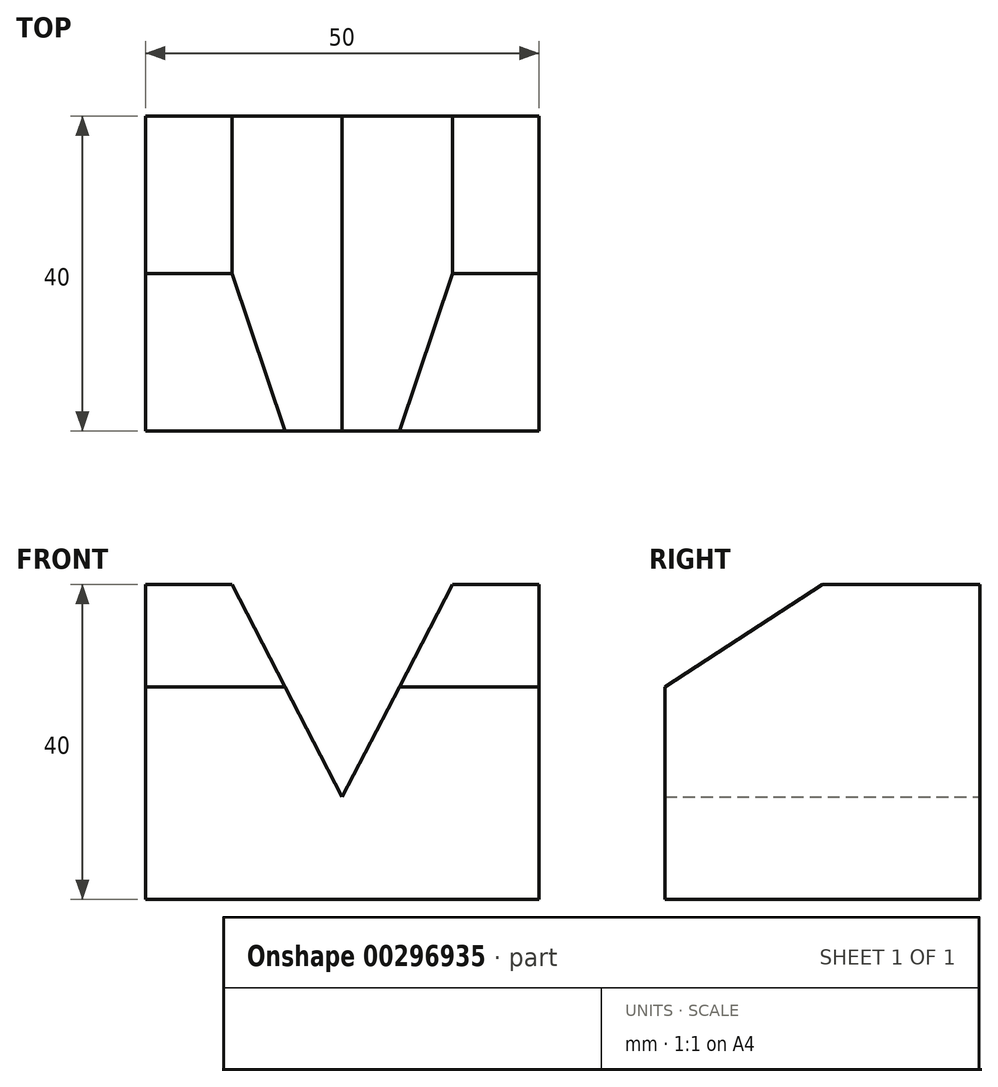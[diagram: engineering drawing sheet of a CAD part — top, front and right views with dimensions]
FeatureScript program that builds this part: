
annotation { "Feature Type Name" : "Feature", "Feature Type Description" : "" }
export const myFeature = defineFeature(function(context is Context, id is Id, definition is map)
    precondition{}
    {
        {
            var Q0;
            Q0=qCreatedBy(makeId("Right.planeOp"),FACE);
            var sketch = newSketch(context, id + "F0", { "sketchPlane" : qUnion([Q0])});
            skLineSegment(sketch, "E0.bottom", {"start": v(0, 0) * mm, "end": v(40, 0) * mm});
            skLineSegment(sketch, "E0.top", {"start": v(0, 40) * mm, "end": v(40, 40) * mm});
            skLineSegment(sketch, "E0.left", {"start": v(0, 0) * mm, "end": v(0, 40) * mm});
            skLineSegment(sketch, "E0.right", {"start": v(40, 0) * mm, "end": v(40, 40) * mm});
            skLineSegment(sketch, "E1", {"start": v(20, 40) * mm, "end": v(0, 27) * mm});
            skSolve(sketch);
        }
        {
            var Q0;
            {var subQ1=sQuery(id+"F0.wireOp",EDGE,"E0.bottom");Q0=makeQuery(id+"F0.imprint","IMPRINT",FACE,{"disambiguationData":[TD([[makeQuery(id+"F0.imprint","IMPRINT",EDGE,{"derivedFrom":subQ1}),1.0]])]});}
            extrude(context, id + "F1", {"entities" : qUnion([Q0]), "depth" : 50 * mm, "symmetric" : true});
        }
        {
            var Q0;
            Q0=makeQuery(id+"F1.opExtrude","SWEPT_FACE",FACE,{"disambiguationData":[OSD([sQuery(id+"F0.wireOp",EDGE,"E0.right")])]});
            var sketch = newSketch(context, id + "F2", { "sketchPlane" : qUnion([Q0])});
            skLineSegment(sketch, "E2", {"start": v(-14, 40) * mm, "end": v(0, 13) * mm});
            skLineSegment(sketch, "E3", {"start": v(0, 13) * mm, "end": v(14, 40) * mm});
            skSolve(sketch);
        }
        {
            var Q0;
            {var subQ0=sQuery(id+"F2.wireOp",EDGE,"E2");Q0=makeQuery(id+"F2.imprint","IMPRINT",FACE,{"disambiguationData":[TD([[makeQuery(id+"F2.imprint","IMPRINT",EDGE,{"derivedFrom":subQ0}),1.0]])]});}
            extrude(context, id + "F3", {"entities" : qUnion([Q0]), "operationType" : NewBodyOperationType.REMOVE, "endBound" : BoundingType.THROUGH_ALL, "oppositeDirection" : true, "depth" : 25 * mm});
        }
    });
